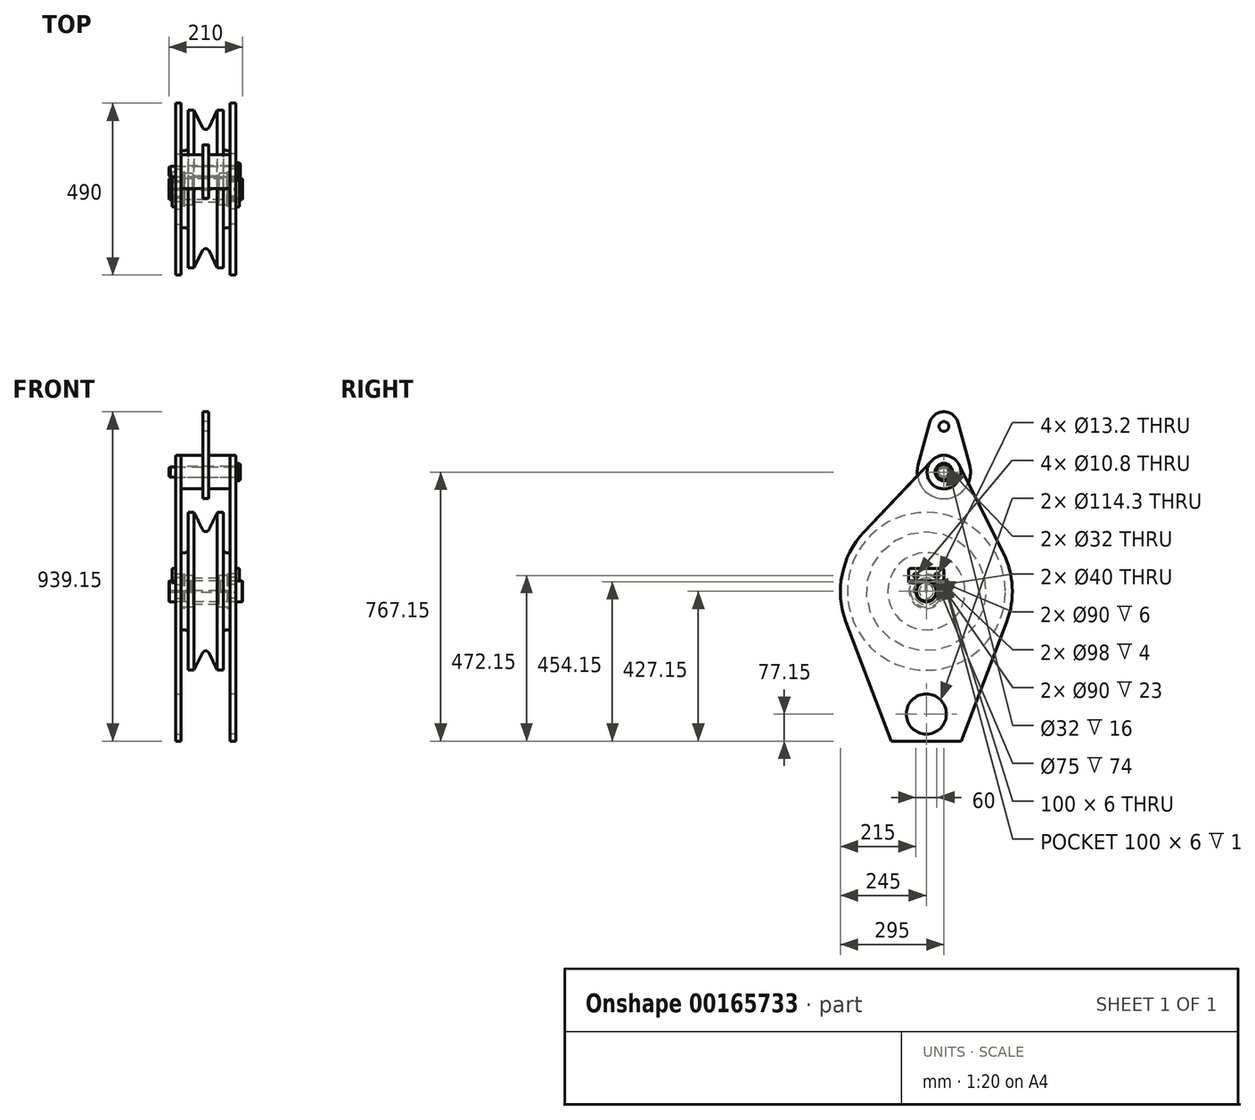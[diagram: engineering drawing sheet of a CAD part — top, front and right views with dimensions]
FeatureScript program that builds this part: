
annotation { "Feature Type Name" : "Feature", "Feature Type Description" : "" }
export const myFeature = defineFeature(function(context is Context, id is Id, definition is map)
    precondition{}
    {
        {
            assignVariable(context, id + "F0", {"name" : "B5", "anyValue" : 16});
        }
        {
            var Q0;
            Q0=qCreatedBy(makeId("Front.planeOp"),FACE);
            var sketch = newSketch(context, id + "F1", { "sketchPlane" : qUnion([Q0])});
            skLineSegment(sketch, "E0", {"start": v(-95.23, 0) * mm, "end": v(95.23, 0) * mm, "construction": true});
            skLineSegment(sketch, "E1", {"start": v(0, 0) * mm, "end": v(0, 256.82) * mm, "construction": true});
            skLineSegment(sketch, "E2", {"start": v(-70, 45) * mm, "end": v(-64, 45) * mm});
            skLineSegment(sketch, "E3", {"start": v(-70, 45) * mm, "end": v(-70, 110) * mm});
            skLineSegment(sketch, "E4", {"start": v(-70, 110) * mm, "end": v(-60, 110) * mm});
            skLineSegment(sketch, "E5", {"start": v(-50, 120) * mm, "end": v(-50, 225) * mm});
            skLineSegment(sketch, "E6", {"start": v(-50, 225) * mm, "end": v(-33.07, 225) * mm});
            skLineSegment(sketch, "E7", {"start": v(-33.07, 225) * mm, "end": v(-8.99, 175.62) * mm});
            skLineSegment(sketch, "E8.MirrorCS", {"start": v(33.07, 225) * mm, "end": v(8.99, 175.62) * mm});
            skLineSegment(sketch, "E9.MirrorCS", {"start": v(50, 225) * mm, "end": v(33.07, 225) * mm});
            skLineSegment(sketch, "E10.MirrorCS", {"start": v(50, 120) * mm, "end": v(50, 225) * mm});
            skLineSegment(sketch, "E11.MirrorCS", {"start": v(70, 110) * mm, "end": v(60, 110) * mm});
            skLineSegment(sketch, "E12.MirrorCS", {"start": v(70, 45) * mm, "end": v(70, 110) * mm});
            skPoint(sketch, "E13.visualSharp", {"position": v(0, 157.19) * mm});
            skArc(sketch, "E13.filletArc", {"start": v(-8.99, 175.62) * mm, "mid": v(0, 170) * mm, "end": v(8.99, 175.62) * mm});
            skPoint(sketch, "E14.visualSharp", {"position": v(-50, 110) * mm});
            skArc(sketch, "E14.filletArc", {"start": v(-60, 110) * mm, "mid": v(-52.93, 112.93) * mm, "end": v(-50, 120) * mm});
            skPoint(sketch, "E15.visualSharp", {"position": v(50, 110) * mm});
            skArc(sketch, "E15.filletArc", {"start": v(50, 120) * mm, "mid": v(52.93, 112.93) * mm, "end": v(60, 110) * mm});
            skLineSegment(sketch, "E16", {"start": v(-64, 45) * mm, "end": v(-64, 49) * mm});
            skLineSegment(sketch, "E17", {"start": v(-64, 49) * mm, "end": v(-60, 49) * mm});
            skLineSegment(sketch, "E18", {"start": v(-60, 49) * mm, "end": v(-60, 45) * mm});
            skLineSegment(sketch, "E19", {"start": v(-37, 45) * mm, "end": v(-37, 37.5) * mm});
            skLineSegment(sketch, "E20", {"start": v(-37, 37.5) * mm, "end": v(37, 37.5) * mm});
            skLineSegment(sketch, "E21", {"start": v(37, 37.5) * mm, "end": v(37, 45) * mm});
            skLineSegment(sketch, "E22", {"start": v(60, 45) * mm, "end": v(60, 49) * mm});
            skLineSegment(sketch, "E23", {"start": v(60, 49) * mm, "end": v(64, 49) * mm});
            skLineSegment(sketch, "E24", {"start": v(64, 49) * mm, "end": v(64, 45) * mm});
            skLineSegment(sketch, "E25.trimOffspring", {"start": v(37, 45) * mm, "end": v(60, 45) * mm});
            skLineSegment(sketch, "E26.trimOffspring", {"start": v(-60, 45) * mm, "end": v(-37, 45) * mm});
            skLineSegment(sketch, "E27.trimOffspring", {"start": v(64, 45) * mm, "end": v(70, 45) * mm});
            skSolve(sketch);
        }
        {
            var Q0;
            {var subQ0=sQuery(id+"F1.wireOp",EDGE,"E3");Q0=makeQuery(id+"F1.imprint","IMPRINT",FACE,{"disambiguationData":[TD([[makeQuery(id+"F1.imprint","IMPRINT",EDGE,{"derivedFrom":subQ0}),-1.0]])]});}
            var Q1;
            Q1=sQuery(id+"F1.wireOp",EDGE,"E0");
            revolve(context, id + "F2", {"entities" : qUnion([Q0]), "axis" : qUnion([Q1]), "revolveType" : RevolveType.FULL});
        }
        {
            var Q0;
            Q0=makeQuery(id+"F2.opRevolve","SWEPT_FACE",FACE,{"disambiguationData":[OSD([sQuery(id+"F1.wireOp",EDGE,"E3")])]});
            var sketch = newSketch(context, id + "F3", { "sketchPlane" : qUnion([Q0])});
            skArc(sketch, "E28", {"start": v(-219.05, 109.74) * mm, "mid": v(-244.68, 12.47) * mm, "end": v(-229.07, -86.9) * mm});
            skCircle(sketch, "E29", {"center": v(0, -350) * mm, "radius": 57.15 * mm});
            skCircle(sketch, "E30", {"center": v(-50, 340) * mm, "radius": 16 * mm});
            skArc(sketch, "E31", {"start": v(-15.1, 372.95) * mm, "mid": v(-56.98, 387.49) * mm, "end": v(-92.92, 361.5) * mm});
            skLineSegment(sketch, "E32", {"start": v(-100, -427.15) * mm, "end": v(100, -427.15) * mm});
            skLineSegment(sketch, "E33", {"start": v(100, -427.15) * mm, "end": v(229.07, -86.9) * mm});
            skLineSegment(sketch, "E34", {"start": v(-100, -427.15) * mm, "end": v(-229.07, -86.9) * mm});
            skLineSegment(sketch, "E35", {"start": v(-219.05, 109.74) * mm, "end": v(-92.92, 361.5) * mm});
            skLineSegment(sketch, "E36", {"start": v(-15.1, 372.95) * mm, "end": v(178.18, 168.16) * mm});
            skLineSegment(sketch, "E37", {"start": v(0, -350) * mm, "end": v(0, -427.15) * mm, "construction": true});
            skArc(sketch, "E38.trimOffspring", {"start": v(229.07, -86.9) * mm, "mid": v(240.26, 47.94) * mm, "end": v(178.18, 168.16) * mm});
            skCircle(sketch, "E39", {"center": v(0, 0) * mm, "radius": 20 * mm});
            skSolve(sketch);
        }
        {
            var Q0;
            Q0=makeQuery(id+"F3.imprint","IMPRINT",FACE,{"disambiguationData":[TD([[makeQuery(id+"F3.imprint","IMPRINT",EDGE,{"derivedFrom":sQuery(id+"F3.wireOp",EDGE,"E39")}),-1.0]])]});
            var Q1;
            {var subQ0=sQuery(id+"F1.wireOp",EDGE,"E3");Q1=makeQuery(id+"F3.imprint","IMPRINT",FACE,{"disambiguationData":[TD([[makeQuery(id+"F3.imprint","IMPRINT",EDGE,{"derivedFrom":makeQuery(id+"F2.opRevolve","SWEPT_EDGE",EDGE,{"disambiguationData":[OSD([sQuery(id+"F1.wireOp",EDGE,"E2"),subQ0])]})}),-1.0]])]});}
            var Q2;
            Q2=makeQuery(id+"F3.imprint","IMPRINT",FACE,{"disambiguationData":[TD([[makeQuery(id+"F3.imprint","IMPRINT",EDGE,{"derivedFrom":sQuery(id+"F3.wireOp",EDGE,"E28")}),1.0]])]});
            extrude(context, id + "F4", {"entities" : qUnion([Q0, Q1, Q2]), "depth" : (getVariable(context, 'B5')) * mm});
        }
        {
            var Q0;
            Q0=makeQuery(id+"F4.opExtrude","CAP_FACE",FACE,{"disambiguationData":[OSD([sQuery(id+"F1.wireOp",EDGE,"c1hZ7EjC-oA1p-lxnu-OyGv-p68KHBZepdHb.top"),sQuery(id+"F1.wireOp",EDGE,"c1hZ7EjC-oA1p-lxnu-OyGv-p68KHBZepdHb.left"),sQuery(id+"F3.wireOp",EDGE,"E28"),sQuery(id+"F3.wireOp",EDGE,"E29"),sQuery(id+"F3.wireOp",EDGE,"E30"),sQuery(id+"F3.wireOp",EDGE,"E31"),sQuery(id+"F3.wireOp",EDGE,"E32"),sQuery(id+"F3.wireOp",EDGE,"E33"),sQuery(id+"F3.wireOp",EDGE,"E34"),sQuery(id+"F3.wireOp",EDGE,"E35"),sQuery(id+"F3.wireOp",EDGE,"E36"),sQuery(id+"F3.wireOp",EDGE,"E38.trimOffspring")])],"isStart":false});
            var sketch = newSketch(context, id + "F5", { "sketchPlane" : qUnion([Q0])});
            skLineSegment(sketch, "E40.bottom", {"start": v(-45, 65) * mm, "end": v(45, 65) * mm});
            skLineSegment(sketch, "E40.top", {"start": v(-45, 25) * mm, "end": v(45, 25) * mm});
            skLineSegment(sketch, "E40.left", {"start": v(-50, 60) * mm, "end": v(-50, 30) * mm});
            skLineSegment(sketch, "E40.right", {"start": v(50, 60) * mm, "end": v(50, 30) * mm});
            skPoint(sketch, "E41", {"position": v(-30, 45) * mm});
            skPoint(sketch, "E42", {"position": v(30, 45) * mm});
            skLineSegment(sketch, "E43", {"start": v(-50, 45) * mm, "end": v(50, 45) * mm, "construction": true});
            skPoint(sketch, "E44.visualSharp", {"position": v(-50, 65) * mm});
            skArc(sketch, "E44.filletArc", {"start": v(-45, 65) * mm, "mid": v(-48.54, 63.54) * mm, "end": v(-50, 60) * mm});
            skPoint(sketch, "E45.visualSharp", {"position": v(50, 65) * mm});
            skArc(sketch, "E45.filletArc", {"start": v(50, 60) * mm, "mid": v(48.54, 63.54) * mm, "end": v(45, 65) * mm});
            skPoint(sketch, "E46.visualSharp", {"position": v(50, 25) * mm});
            skArc(sketch, "E46.filletArc", {"start": v(45, 25) * mm, "mid": v(48.54, 26.46) * mm, "end": v(50, 30) * mm});
            skPoint(sketch, "E47.visualSharp", {"position": v(-50, 25) * mm});
            skArc(sketch, "E47.filletArc", {"start": v(-50, 30) * mm, "mid": v(-48.54, 26.46) * mm, "end": v(-45, 25) * mm});
            skSolve(sketch);
        }
        {
            var Q0;
            Q0=makeQuery(id+"F5.imprint","IMPRINT",FACE,{"disambiguationData":[TD([[makeQuery(id+"F5.imprint","IMPRINT",EDGE,{"derivedFrom":sQuery(id+"F5.wireOp",EDGE,"E40.bottom")}),-1.0]])]});
            var Q1;
            {var subQ0=sQuery(id+"F5.wireOp",EDGE,"E40.top");var subQ1=makeQuery(id+"F4.opExtrude","CAP_EDGE",EDGE,{"disambiguationData":[OSD([sQuery(id+"F1.wireOp",EDGE,"c1hZ7EjC-oA1p-lxnu-OyGv-p68KHBZepdHb.top"),sQuery(id+"F1.wireOp",EDGE,"c1hZ7EjC-oA1p-lxnu-OyGv-p68KHBZepdHb.left")])],"isStart":false});var subQ2=makeQuery(id+"F5.imprint","INTERSECT",VERTEX,{"disambiguationData":[OD(0.0)],"derivedFrom":[subQ1,subQ0]});Q1=makeQuery(id+"F5.imprint","IMPRINT",FACE,{"disambiguationData":[TD([[makeQuery(id+"F5.imprint","IMPRINT",EDGE,{"disambiguationData":[TD([[subQ2,-1.0]])],"derivedFrom":subQ0}),1.0]])]});}
            extrude(context, id + "F6", {"entities" : qUnion([Q0, Q1]), "depth" : 10 * mm});
        }
        {
            var Q0;
            Q0=sQuery(id+"F5.wireOp",VERTEX,"E41");
            var Q1;
            Q1=sQuery(id+"F5.wireOp",VERTEX,"E42");
            var Q2;
            Q2=makeQuery(id+"F4.opExtrude","SWEPT_BODY",BODY,{"disambiguationData":[OSD([sQuery(id+"F1.wireOp",EDGE,"c1hZ7EjC-oA1p-lxnu-OyGv-p68KHBZepdHb.top"),sQuery(id+"F1.wireOp",EDGE,"c1hZ7EjC-oA1p-lxnu-OyGv-p68KHBZepdHb.left"),sQuery(id+"F3.wireOp",EDGE,"E28"),sQuery(id+"F3.wireOp",EDGE,"E29"),sQuery(id+"F3.wireOp",EDGE,"E30"),sQuery(id+"F3.wireOp",EDGE,"E31"),sQuery(id+"F3.wireOp",EDGE,"E32"),sQuery(id+"F3.wireOp",EDGE,"E33"),sQuery(id+"F3.wireOp",EDGE,"E34"),sQuery(id+"F3.wireOp",EDGE,"E35"),sQuery(id+"F3.wireOp",EDGE,"E36"),sQuery(id+"F3.wireOp",EDGE,"E38.trimOffspring")])]});
            hole(context, id + "F7", {"style" : HoleStyle.SIMPLE, "endStyle" : HoleEndStyle.THROUGH, "standardTappedOrClearance" : lookupTablePath({ "standard" : "ISO", "engagement" : "75%", "pitch" : "1.25 mm", "size" : "M12", "type" : "Tapped" }), "standardBlindInLast" : lookupTablePath({ "standard" : "ISO", "engagement" : "75%", "pitch" : "1.25 mm", "size" : "M12", "type" : "Tapped" }), "holeDiameter" : 10.8 * mm, "locations" : qUnion([Q0, Q1]), "scope" : qUnion([Q2]), "isTappedThrough" : true, "majorDiameter" : 12 * mm, "showTappedDepth" : true});
        }
        {
            var Q0;
            Q0=sQuery(id+"F5.wireOp",VERTEX,"E41");
            var Q1;
            Q1=sQuery(id+"F5.wireOp",VERTEX,"E42");
            var Q2;
            Q2=makeQuery(id+"F6.opExtrude","SWEPT_BODY",BODY,{"disambiguationData":[OSD([sQuery(id+"F5.wireOp",EDGE,"E40.bottom"),sQuery(id+"F5.wireOp",EDGE,"E40.top"),sQuery(id+"F5.wireOp",EDGE,"E40.left"),sQuery(id+"F5.wireOp",EDGE,"E40.right"),sQuery(id+"F5.wireOp",EDGE,"E44.filletArc"),sQuery(id+"F5.wireOp",EDGE,"E45.filletArc"),sQuery(id+"F5.wireOp",EDGE,"E46.filletArc"),sQuery(id+"F5.wireOp",EDGE,"E47.filletArc")])]});
            hole(context, id + "F8", {"style" : HoleStyle.SIMPLE, "endStyle" : HoleEndStyle.THROUGH, "oppositeDirection" : true, "standardTappedOrClearance" : lookupTablePath({ "standard" : "ISO", "fit" : "Normal", "size" : "M12", "type" : "Clearance" }), "standardBlindInLast" : lookupTablePath({ "fit" : "Standard", "standard" : "ISO", "size" : "M12", "type" : "Clearance" }), "holeDiameter" : 13.2 * mm, "locations" : qUnion([Q0, Q1]), "scope" : qUnion([Q2]), "isTappedThrough" : true});
        }
        {
            var Q0;
            Q0=qCreatedBy(makeId("Right.planeOp"),FACE);
            var sketch = newSketch(context, id + "F9", { "sketchPlane" : qUnion([Q0])});
            skCircle(sketch, "E48", {"center": v(0, 0) * mm, "radius": 30 * mm});
            skCircle(sketch, "E49", {"center": v(50, 340) * mm, "radius": 16 * mm});
            skCircle(sketch, "E50", {"center": v(50, 340) * mm, "radius": 48 * mm});
            skArc(sketch, "E51", {"start": v(-23.35, 359.88) * mm, "mid": v(50, 264) * mm, "end": v(123.35, 359.88) * mm});
            skCircle(sketch, "E52", {"center": v(50, 470) * mm, "radius": 14 * mm});
            skArc(sketch, "E53", {"start": v(90.54, 480.98) * mm, "mid": v(50, 512) * mm, "end": v(9.46, 480.98) * mm});
            skLineSegment(sketch, "E54", {"start": v(123.35, 359.88) * mm, "end": v(90.54, 480.98) * mm});
            skLineSegment(sketch, "E55", {"start": v(9.46, 480.98) * mm, "end": v(-23.35, 359.88) * mm});
            skSolve(sketch);
        }
        {
            var Q0;
            Q0=makeQuery(id+"F9.imprint","IMPRINT",FACE,{"disambiguationData":[TD([[makeQuery(id+"F9.imprint","IMPRINT",EDGE,{"derivedFrom":sQuery(id+"F9.wireOp",EDGE,"E48")}),1.0]])]});
            extrude(context, id + "F10", {"entities" : qUnion([Q0]), "depth" : 210 * mm, "symmetric" : true});
        }
        {
            var Q0;
            Q0=makeQuery(id+"F10.opExtrude","CAP_EDGE",EDGE,{"disambiguationData":[OSD([sQuery(id+"F9.wireOp",EDGE,"E48")])],"isStart":true});
            var Q1;
            Q1=makeQuery(id+"F10.opExtrude","CAP_EDGE",EDGE,{"disambiguationData":[OSD([sQuery(id+"F9.wireOp",EDGE,"E48")])],"isStart":false});
            chamfer(context, id + "F11", {"entities" : qUnion([Q0, Q1]), "width" : 2 * mm, "tangentPropagation" : true});
        }
        {
            var Q0;
            Q0=qCreatedBy(makeId("Front.planeOp"),FACE);
            var sketch = newSketch(context, id + "F12", { "sketchPlane" : qUnion([Q0])});
            skLineSegment(sketch, "E56", {"start": v(-85, 30) * mm, "end": v(-85, 24) * mm});
            skLineSegment(sketch, "E57", {"start": v(-85, 24) * mm, "end": v(-97, 24) * mm});
            skLineSegment(sketch, "E58", {"start": v(-97, 24) * mm, "end": v(-97, 30) * mm});
            skLineSegment(sketch, "E59", {"start": v(-97, 30) * mm, "end": v(-85, 30) * mm});
            skSolve(sketch);
        }
        {
            var Q0;
            Q0=makeQuery(id+"F12.imprint","IMPRINT",FACE,{"disambiguationData":[TD([[makeQuery(id+"F12.imprint","IMPRINT",EDGE,{"derivedFrom":sQuery(id+"F12.wireOp",EDGE,"E56")}),-1.0]])]});
            extrude(context, id + "F13", {"entities" : qUnion([Q0]), "operationType" : NewBodyOperationType.REMOVE, "oppositeDirection" : true, "depth" : 100 * mm, "symmetric" : true});
        }
        {
            var Q0;
            Q0=makeQuery(id+"F10.opExtrude","CAP_FACE",FACE,{"disambiguationData":[OSD([sQuery(id+"F9.wireOp",EDGE,"E48")])],"isStart":true});
            var sketch = newSketch(context, id + "F14", { "sketchPlane" : qUnion([Q0])});
            skPoint(sketch, "E60", {"position": v(0, 0) * mm});
            skSolve(sketch);
        }
        {
            var Q0;
            Q0=sQuery(id+"F14.wireOp",VERTEX,"E60");
            var Q1;
            Q1=makeQuery(id+"F10.opExtrude","SWEPT_BODY",BODY,{"disambiguationData":[OSD([sQuery(id+"F9.wireOp",EDGE,"E48")])]});
            hole(context, id + "F15", {"style" : HoleStyle.SIMPLE, "endStyle" : HoleEndStyle.BLIND, "standardTappedOrClearance" : lookupTablePath({ "standard" : "ISO", "size" : "4", "type" : "Drilled" }), "standardBlindInLast" : lookupTablePath({ "standard" : "ISO", "size" : "4", "type" : "Drilled" }), "holeDiameter" : 4 * mm, "holeDepth" : 180 * mm, "locations" : qUnion([Q0]), "scope" : qUnion([Q1])});
        }
        {
            var Q0;
            Q0=sQuery(id+"F14.wireOp",VERTEX,"E60");
            var Q1;
            Q1=makeQuery(id+"F10.opExtrude","SWEPT_BODY",BODY,{"disambiguationData":[OSD([sQuery(id+"F9.wireOp",EDGE,"E48")])]});
            hole(context, id + "F16", {"style" : HoleStyle.SIMPLE, "endStyle" : HoleEndStyle.BLIND, "standardTappedOrClearance" : lookupTablePath({ "standard" : "ISO", "engagement" : "75%", "pitch" : "0.75 mm", "size" : "M6", "type" : "Tapped" }), "standardBlindInLast" : lookupTablePath({ "standard" : "ISO", "engagement" : "75%", "pitch" : "0.75 mm", "size" : "M6", "type" : "Tapped" }), "holeDiameter" : 5.25 * mm, "holeDepth" : 10 * mm, "locations" : qUnion([Q0]), "scope" : qUnion([Q1]), "majorDiameter" : 6 * mm});
        }
        {
            var Q0;
            Q0=qCreatedBy(makeId("Top.planeOp"),FACE);
            var sketch = newSketch(context, id + "F17", { "sketchPlane" : qUnion([Q0])});
            skPoint(sketch, "E61", {"position": v(-40, 0) * mm});
            skPoint(sketch, "E62", {"position": v(40, 0) * mm});
            skSolve(sketch);
        }
        {
            var Q0;
            Q0=sQuery(id+"F17.wireOp",VERTEX,"E61");
            var Q1;
            Q1=sQuery(id+"F17.wireOp",VERTEX,"E62");
            var Q2;
            Q2=makeQuery(id+"F10.opExtrude","SWEPT_BODY",BODY,{"disambiguationData":[OSD([sQuery(id+"F9.wireOp",EDGE,"E48")])]});
            hole(context, id + "F18", {"style" : HoleStyle.SIMPLE, "endStyle" : HoleEndStyle.THROUGH, "oppositeDirection" : true, "standardTappedOrClearance" : lookupTablePath({ "standard" : "ISO", "fit" : "Normal", "size" : "M4", "type" : "Clearance" }), "standardBlindInLast" : lookupTablePath({ "fit" : "Standard", "standard" : "ISO", "size" : "M4", "type" : "Clearance" }), "holeDiameter" : 4.4 * mm, "locations" : qUnion([Q0, Q1]), "scope" : qUnion([Q2]), "isTappedThrough" : true});
        }
        {
            var Q0;
            Q0=makeQuery(id+"F4.opExtrude","SWEPT_BODY",BODY,{"disambiguationData":[OSD([sQuery(id+"F1.wireOp",EDGE,"c1hZ7EjC-oA1p-lxnu-OyGv-p68KHBZepdHb.top"),sQuery(id+"F1.wireOp",EDGE,"c1hZ7EjC-oA1p-lxnu-OyGv-p68KHBZepdHb.left"),sQuery(id+"F3.wireOp",EDGE,"E28"),sQuery(id+"F3.wireOp",EDGE,"E29"),sQuery(id+"F3.wireOp",EDGE,"E30"),sQuery(id+"F3.wireOp",EDGE,"E31"),sQuery(id+"F3.wireOp",EDGE,"E32"),sQuery(id+"F3.wireOp",EDGE,"E33"),sQuery(id+"F3.wireOp",EDGE,"E34"),sQuery(id+"F3.wireOp",EDGE,"E35"),sQuery(id+"F3.wireOp",EDGE,"E36"),sQuery(id+"F3.wireOp",EDGE,"E38.trimOffspring")])]});
            var Q1;
            Q1=makeQuery(id+"F6.opExtrude","SWEPT_BODY",BODY,{"disambiguationData":[OSD([sQuery(id+"F5.wireOp",EDGE,"E40.bottom"),sQuery(id+"F5.wireOp",EDGE,"E40.top"),sQuery(id+"F5.wireOp",EDGE,"E40.left"),sQuery(id+"F5.wireOp",EDGE,"E40.right"),sQuery(id+"F5.wireOp",EDGE,"E44.filletArc"),sQuery(id+"F5.wireOp",EDGE,"E45.filletArc"),sQuery(id+"F5.wireOp",EDGE,"E46.filletArc"),sQuery(id+"F5.wireOp",EDGE,"E47.filletArc")])]});
            var Q2;
            Q2=qCreatedBy(makeId("Right.planeOp"),FACE);
            mirror(context, id + "F19", {"entities" : qUnion([Q0, Q1]), "mirrorPlane" : qUnion([Q2])});
        }
        {
            var Q0;
            Q0=makeQuery(id+"F9.imprint","IMPRINT",FACE,{"disambiguationData":[TD([[makeQuery(id+"F9.imprint","IMPRINT",EDGE,{"derivedFrom":sQuery(id+"F9.wireOp",EDGE,"E49")}),-1.0]])]});
            var Q1;
            Q1=makeQuery(id+"F19.opPattern","COPY",FACE,{"derivedFrom":makeQuery(id+"F4.opExtrude","CAP_FACE",FACE,{"disambiguationData":[OSD([sQuery(id+"F1.wireOp",EDGE,"c1hZ7EjC-oA1p-lxnu-OyGv-p68KHBZepdHb.top"),sQuery(id+"F1.wireOp",EDGE,"c1hZ7EjC-oA1p-lxnu-OyGv-p68KHBZepdHb.left"),sQuery(id+"F3.wireOp",EDGE,"E28"),sQuery(id+"F3.wireOp",EDGE,"E29"),sQuery(id+"F3.wireOp",EDGE,"E30"),sQuery(id+"F3.wireOp",EDGE,"E31"),sQuery(id+"F3.wireOp",EDGE,"E32"),sQuery(id+"F3.wireOp",EDGE,"E33"),sQuery(id+"F3.wireOp",EDGE,"E34"),sQuery(id+"F3.wireOp",EDGE,"E35"),sQuery(id+"F3.wireOp",EDGE,"E36"),sQuery(id+"F3.wireOp",EDGE,"E38.trimOffspring")])],"isStart":true}),"instanceName":"1"});
            var Q2;
            Q2=makeQuery(id+"F4.opExtrude","CAP_FACE",FACE,{"disambiguationData":[OSD([sQuery(id+"F1.wireOp",EDGE,"c1hZ7EjC-oA1p-lxnu-OyGv-p68KHBZepdHb.top"),sQuery(id+"F1.wireOp",EDGE,"c1hZ7EjC-oA1p-lxnu-OyGv-p68KHBZepdHb.left"),sQuery(id+"F3.wireOp",EDGE,"E28"),sQuery(id+"F3.wireOp",EDGE,"E29"),sQuery(id+"F3.wireOp",EDGE,"E30"),sQuery(id+"F3.wireOp",EDGE,"E31"),sQuery(id+"F3.wireOp",EDGE,"E32"),sQuery(id+"F3.wireOp",EDGE,"E33"),sQuery(id+"F3.wireOp",EDGE,"E34"),sQuery(id+"F3.wireOp",EDGE,"E35"),sQuery(id+"F3.wireOp",EDGE,"E36"),sQuery(id+"F3.wireOp",EDGE,"E38.trimOffspring")])],"isStart":true});
            extrude(context, id + "F20", {"entities" : qUnion([Q0]), "endBound" : BoundingType.UP_TO_SURFACE, "endBoundEntityFace" : qUnion([Q1]), "depth" : 25 * mm, "hasSecondDirection" : true, "secondDirectionBound" : BoundingType.UP_TO_SURFACE, "secondDirectionOppositeDirection" : true, "secondDirectionBoundEntityFace" : qUnion([Q2]), "secondDirectionDepth" : 25 * mm});
        }
        {
            var Q0;
            Q0=makeQuery(id+"F9.imprint","IMPRINT",FACE,{"disambiguationData":[TD([[makeQuery(id+"F9.imprint","IMPRINT",EDGE,{"derivedFrom":sQuery(id+"F9.wireOp",EDGE,"E50")}),-1.0]])]});
            extrude(context, id + "F21", {"entities" : qUnion([Q0]), "operationType" : NewBodyOperationType.ADD, "depth" : (getVariable(context, 'B5')) * mm, "symmetric" : true});
        }
        {
            var Q0;
            Q0=makeQuery(id+"F19.opPattern","COPY",FACE,{"derivedFrom":makeQuery(id+"F4.opExtrude","CAP_FACE",FACE,{"disambiguationData":[OSD([sQuery(id+"F3.wireOp",EDGE,"E28"),sQuery(id+"F3.wireOp",EDGE,"E29"),sQuery(id+"F3.wireOp",EDGE,"E30"),sQuery(id+"F3.wireOp",EDGE,"E31"),sQuery(id+"F3.wireOp",EDGE,"E32"),sQuery(id+"F3.wireOp",EDGE,"E33"),sQuery(id+"F3.wireOp",EDGE,"E34"),sQuery(id+"F3.wireOp",EDGE,"E35"),sQuery(id+"F3.wireOp",EDGE,"E36"),sQuery(id+"F3.wireOp",EDGE,"E38.trimOffspring"),sQuery(id+"F3.wireOp",EDGE,"E39")])],"isStart":false}),"instanceName":"1"});
            var sketch = newSketch(context, id + "F22", { "sketchPlane" : qUnion([Q0])});
            skCircle(sketch, "E63", {"center": v(50, 340) * mm, "radius": 15 * mm});
            skCircle(sketch, "E64", {"center": v(50, 340) * mm, "radius": 25 * mm});
            skSolve(sketch);
        }
        {
            var Q0;
            Q0=makeQuery(id+"F22.imprint","IMPRINT",FACE,{"disambiguationData":[TD([[makeQuery(id+"F22.imprint","IMPRINT",EDGE,{"derivedFrom":sQuery(id+"F22.wireOp",EDGE,"E63")}),1.0]])]});
            extrude(context, id + "F23", {"entities" : qUnion([Q0]), "oppositeDirection" : true, "depth" : 190 * mm});
        }
        {
            var Q0;
            Q0=makeQuery(id+"F22.imprint","IMPRINT",FACE,{"disambiguationData":[TD([[makeQuery(id+"F22.imprint","IMPRINT",EDGE,{"derivedFrom":sQuery(id+"F22.wireOp",EDGE,"E63")}),1.0]])]});
            var Q1;
            Q1=makeQuery(id+"F22.imprint","IMPRINT",FACE,{"disambiguationData":[TD([[makeQuery(id+"F22.imprint","IMPRINT",EDGE,{"derivedFrom":sQuery(id+"F22.wireOp",EDGE,"E64")}),1.0]])]});
            var Q2;
            Q2=makeQuery(id+"F22.imprint","IMPRINT",FACE,{"disambiguationData":[TD([[makeQuery(id+"F22.imprint","IMPRINT",EDGE,{"derivedFrom":sQuery(id+"F22.wireOp",EDGE,"E63")}),-1.0]])]});
            extrude(context, id + "F24", {"entities" : qUnion([Q0, Q1, Q2]), "operationType" : NewBodyOperationType.ADD, "depth" : 12 * mm});
        }
        {
            var Q0;
            Q0=makeQuery(id+"F24.opExtrude","CAP_EDGE",EDGE,{"disambiguationData":[OSD([sQuery(id+"F22.wireOp",EDGE,"E64")])],"isStart":false});
            var Q1;
            Q1=makeQuery(id+"F24.opExtrude","CAP_EDGE",EDGE,{"disambiguationData":[OSD([sQuery(id+"F22.wireOp",EDGE,"E64")])],"isStart":true});
            var Q2;
            Q2=makeQuery(id+"F23.opExtrude","CAP_EDGE",EDGE,{"disambiguationData":[OSD([sQuery(id+"F22.wireOp",EDGE,"E63")])],"isStart":false});
            chamfer(context, id + "F25", {"entities" : qUnion([Q0, Q1, Q2]), "width" : 3 * mm, "tangentPropagation" : true});
        }
    });
